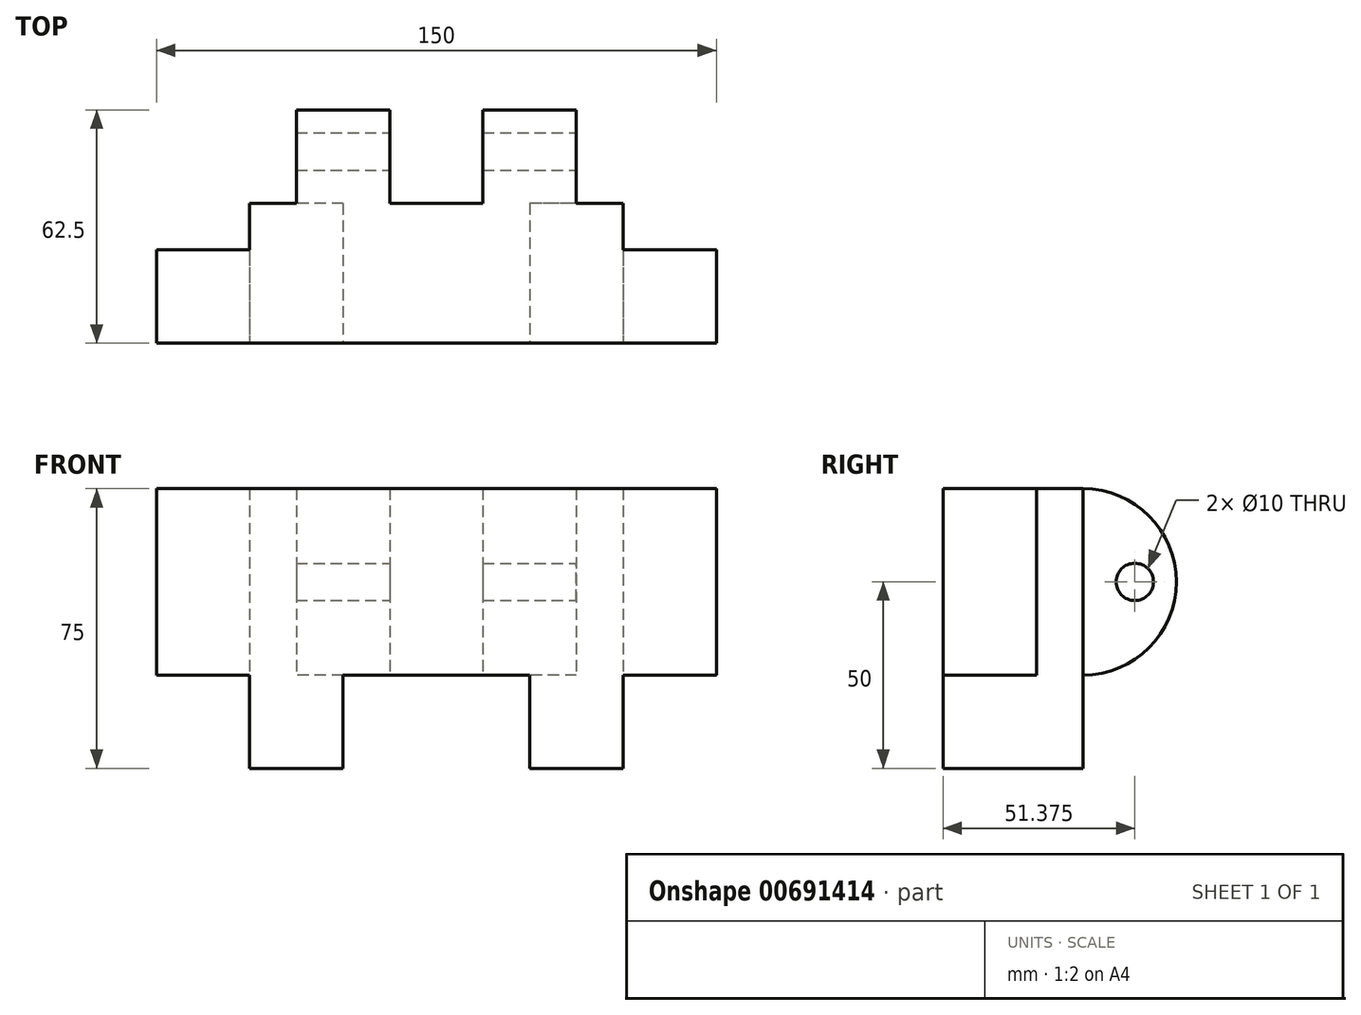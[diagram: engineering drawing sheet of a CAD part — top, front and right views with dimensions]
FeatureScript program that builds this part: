
annotation { "Feature Type Name" : "Feature", "Feature Type Description" : "" }
export const myFeature = defineFeature(function(context is Context, id is Id, definition is map)
    precondition{}
    {
        {
            var Q0;
            Q0=qCreatedBy(makeId("Top.planeOp"),FACE);
            var sketch = newSketch(context, id + "F0", { "sketchPlane" : qUnion([Q0])});
            skLineSegment(sketch, "E0.bottom", {"start": v(75, 12.5) * mm, "end": v(-75, 12.5) * mm});
            skLineSegment(sketch, "E0.top", {"start": v(75, -12.5) * mm, "end": v(-75, -12.5) * mm});
            skLineSegment(sketch, "E0.left", {"start": v(75, 12.5) * mm, "end": v(75, -12.5) * mm});
            skLineSegment(sketch, "E0.right", {"start": v(-75, 12.5) * mm, "end": v(-75, -12.5) * mm});
            skPoint(sketch, "E0.middle", {"position": v(0, 0) * mm});
            skLineSegment(sketch, "E1.bottom", {"start": v(50, 25) * mm, "end": v(-50, 25) * mm});
            skLineSegment(sketch, "E1.top", {"start": v(50, 0) * mm, "end": v(-50, 0) * mm});
            skLineSegment(sketch, "E1.left", {"start": v(50, 25) * mm, "end": v(50, 0) * mm});
            skLineSegment(sketch, "E1.right", {"start": v(-50, 25) * mm, "end": v(-50, 0) * mm});
            skPoint(sketch, "E1.middle", {"position": v(0, 12.5) * mm});
            skSolve(sketch);
        }
        {
            var Q0;
            Q0 = qSketchRegion(id + "F0", true);
            extrude(context, id + "F1", {"entities" : qUnion([Q0]), "depth" : 50 * mm, "offsetDistance" : 25 * mm});
        }
        {
            var Q0;
            Q0=makeQuery(id+"F1.opExtrude","SWEPT_FACE",FACE,{"disambiguationData":[OSD([sQuery(id+"F0.wireOp",EDGE,"E1.bottom")])]});
            var sketch = newSketch(context, id + "F2", { "sketchPlane" : qUnion([Q0])});
            skLineSegment(sketch, "E2.bottom", {"start": v(37.5, 50) * mm, "end": v(-37.5, 50) * mm});
            skLineSegment(sketch, "E2.top", {"start": v(37.5, 0) * mm, "end": v(-37.5, 0) * mm});
            skLineSegment(sketch, "E2.left", {"start": v(37.5, 50) * mm, "end": v(37.5, 0) * mm});
            skLineSegment(sketch, "E2.right", {"start": v(-37.5, 50) * mm, "end": v(-37.5, 0) * mm});
            skPoint(sketch, "E2.middle", {"position": v(0, 25) * mm});
            skPoint(sketch, "E2.middle.positionSnap0", {"position": v(50, 25) * mm});
            skPoint(sketch, "E2.centerSnap0", {"position": v(50, 25) * mm});
            skLineSegment(sketch, "E3.bottom", {"start": v(12.5, 50) * mm, "end": v(-12.5, 50) * mm});
            skLineSegment(sketch, "E3.top", {"start": v(12.5, 0) * mm, "end": v(-12.5, 0) * mm});
            skLineSegment(sketch, "E3.left", {"start": v(12.5, 50) * mm, "end": v(12.5, 0) * mm});
            skLineSegment(sketch, "E3.right", {"start": v(-12.5, 50) * mm, "end": v(-12.5, 0) * mm});
            skSolve(sketch);
        }
        {
            var Q0;
            {var subQ0=sQuery(id+"F2.wireOp",EDGE,"E2.right");Q0=makeQuery(id+"F2.imprint","IMPRINT",FACE,{"disambiguationData":[TD([[makeQuery(id+"F2.imprint","IMPRINT",EDGE,{"derivedFrom":subQ0}),1.0]])]});}
            var Q1;
            {var subQ0=sQuery(id+"F2.wireOp",EDGE,"E2.left");Q1=makeQuery(id+"F2.imprint","IMPRINT",FACE,{"disambiguationData":[TD([[makeQuery(id+"F2.imprint","IMPRINT",EDGE,{"derivedFrom":subQ0}),-1.0]])]});}
            extrude(context, id + "F3", {"entities" : qUnion([Q0, Q1]), "operationType" : NewBodyOperationType.ADD, "depth" : 25 * mm, "offsetDistance" : 25 * mm});
        }
        {
            var Q0;
            {var subQ0=sQuery(id+"F2.wireOp",EDGE,"E2.bottom");Q0=makeQuery(id+"F3.opExtrude","CAP_EDGE",EDGE,{"disambiguationData":[OSD([subQ0]),TDD([makeQuery(id+"F2.imprint","IMPRINT",EDGE,{"disambiguationData":[TD([[makeQuery(id+"F2.imprint","INTERSECT",VERTEX,{"derivedFrom":[makeQuery(id+"F1.opExtrude","CAP_EDGE",EDGE,{"disambiguationData":[OSD([sQuery(id+"F0.wireOp",EDGE,"E1.bottom")])],"isStart":false}),subQ0,sQuery(id+"F2.wireOp",EDGE,"E2.right")]}),-1.0]])],"derivedFrom":subQ0})])],"isStart":false});}
            var Q1;
            {var subQ0=sQuery(id+"F2.wireOp",EDGE,"E2.bottom");Q1=makeQuery(id+"F3.opExtrude","CAP_EDGE",EDGE,{"disambiguationData":[OSD([subQ0]),TDD([makeQuery(id+"F2.imprint","IMPRINT",EDGE,{"disambiguationData":[TD([[makeQuery(id+"F2.imprint","INTERSECT",VERTEX,{"derivedFrom":[makeQuery(id+"F1.opExtrude","CAP_EDGE",EDGE,{"disambiguationData":[OSD([sQuery(id+"F0.wireOp",EDGE,"E1.bottom")])],"isStart":false}),subQ0,sQuery(id+"F2.wireOp",EDGE,"E2.left")]}),1.0]])],"derivedFrom":subQ0})])],"isStart":false});}
            var Q2;
            {var subQ0=sQuery(id+"F2.wireOp",EDGE,"E2.top");Q2=makeQuery(id+"F3.opExtrude","CAP_EDGE",EDGE,{"disambiguationData":[OSD([subQ0]),TDD([makeQuery(id+"F2.imprint","IMPRINT",EDGE,{"disambiguationData":[TD([[makeQuery(id+"F2.imprint","INTERSECT",VERTEX,{"derivedFrom":[makeQuery(id+"F1.opExtrude","CAP_EDGE",EDGE,{"disambiguationData":[OSD([sQuery(id+"F0.wireOp",EDGE,"E1.bottom")])],"isStart":true}),subQ0,sQuery(id+"F2.wireOp",EDGE,"E2.left")]}),1.0]])],"derivedFrom":subQ0})])],"isStart":false});}
            var Q3;
            {var subQ0=sQuery(id+"F2.wireOp",EDGE,"E2.top");Q3=makeQuery(id+"F3.opExtrude","CAP_EDGE",EDGE,{"disambiguationData":[OSD([subQ0]),TDD([makeQuery(id+"F2.imprint","IMPRINT",EDGE,{"disambiguationData":[TD([[makeQuery(id+"F2.imprint","INTERSECT",VERTEX,{"derivedFrom":[makeQuery(id+"F1.opExtrude","CAP_EDGE",EDGE,{"disambiguationData":[OSD([sQuery(id+"F0.wireOp",EDGE,"E1.bottom")])],"isStart":true}),subQ0,sQuery(id+"F2.wireOp",EDGE,"E2.right")]}),-1.0]])],"derivedFrom":subQ0})])],"isStart":false});}
            fillet(context, id + "F4", {"entities" : qUnion([Q0, Q1, Q2, Q3]), "radius" : 25 * mm, "tangentPropagation" : true, "allowEdgeOverflow" : false});
        }
        {
            var Q0;
            Q0=makeQuery(id+"F3.opExtrude","SWEPT_FACE",FACE,{"disambiguationData":[OSD([sQuery(id+"F2.wireOp",EDGE,"E2.right")])]});
            var sketch = newSketch(context, id + "F5", { "sketchPlane" : qUnion([Q0])});
            skCircle(sketch, "E4", {"center": v(38.88, 25) * mm, "radius": 5 * mm});
            skPoint(sketch, "E4.centerSnap0", {"position": v(25, 25) * mm});
            skSolve(sketch);
        }
        {
            var Q0;
            Q0 = qSketchRegion(id + "F5", true);
            extrude(context, id + "F6", {"entities" : qUnion([Q0]), "operationType" : NewBodyOperationType.REMOVE, "endBound" : BoundingType.THROUGH_ALL, "oppositeDirection" : true, "depth" : 25 * mm, "offsetDistance" : 25 * mm});
        }
        {
            var Q0;
            {var subQ0=sQuery(id+"F2.wireOp",EDGE,"E2.bottom");var subQ1=sQuery(id+"F0.wireOp",EDGE,"E1.bottom");var subQ2=makeQuery(id+"F1.opExtrude","CAP_EDGE",EDGE,{"disambiguationData":[OSD([subQ1])],"isStart":false});Q0=makeQuery(id+"F3.boolean.opBoolean","MERGE",FACE,{"derivedFrom":[makeQuery(id+"F1.opExtrude","CAP_FACE",FACE,{"disambiguationData":[OSD([sQuery(id+"F0.wireOp",EDGE,"E0.bottom"),sQuery(id+"F0.wireOp",EDGE,"E0.top"),sQuery(id+"F0.wireOp",EDGE,"E0.left"),sQuery(id+"F0.wireOp",EDGE,"E0.right"),subQ1,sQuery(id+"F0.wireOp",EDGE,"E1.left"),sQuery(id+"F0.wireOp",EDGE,"E1.right")])],"isStart":false}),makeQuery(id+"F3.opExtrude","SWEPT_FACE",FACE,{"disambiguationData":[OSD([subQ0]),TDD([makeQuery(id+"F2.imprint","IMPRINT",EDGE,{"disambiguationData":[TD([[makeQuery(id+"F2.imprint","INTERSECT",VERTEX,{"derivedFrom":[subQ2,subQ0,sQuery(id+"F2.wireOp",EDGE,"E2.right")]}),-1.0]])],"derivedFrom":subQ0})])]}),makeQuery(id+"F3.opExtrude","SWEPT_FACE",FACE,{"disambiguationData":[OSD([subQ0]),TDD([makeQuery(id+"F2.imprint","IMPRINT",EDGE,{"disambiguationData":[TD([[makeQuery(id+"F2.imprint","INTERSECT",VERTEX,{"derivedFrom":[subQ2,subQ0,sQuery(id+"F2.wireOp",EDGE,"E2.left")]}),1.0]])],"derivedFrom":subQ0})])]})]});}
            var sketch = newSketch(context, id + "F7", { "sketchPlane" : qUnion([Q0])});
            skLineSegment(sketch, "E5.bottom", {"start": v(-50, 25) * mm, "end": v(50, 25) * mm});
            skLineSegment(sketch, "E5.top", {"start": v(-50, -12.5) * mm, "end": v(50, -12.5) * mm});
            skLineSegment(sketch, "E5.left", {"start": v(-50, 25) * mm, "end": v(-50, -12.5) * mm});
            skLineSegment(sketch, "E5.right", {"start": v(50, 25) * mm, "end": v(50, -12.5) * mm});
            skLineSegment(sketch, "E6.bottom", {"start": v(-25, 25) * mm, "end": v(25, 25) * mm});
            skLineSegment(sketch, "E6.top", {"start": v(-25, -12.5) * mm, "end": v(25, -12.5) * mm});
            skLineSegment(sketch, "E6.left", {"start": v(-25, 25) * mm, "end": v(-25, -12.5) * mm});
            skLineSegment(sketch, "E6.right", {"start": v(25, 25) * mm, "end": v(25, -12.5) * mm});
            skPoint(sketch, "E6.middle", {"position": v(0, 6.25) * mm});
            skPoint(sketch, "E6.middle.positionSnap0", {"position": v(-50, 6.25) * mm});
            skPoint(sketch, "E6.centerSnap0", {"position": v(-50, 6.25) * mm});
            skLineSegment(sketch, "E7.top", {"start": v(-25, -2.5) * mm, "end": v(25, -2.5) * mm});
            skLineSegment(sketch, "E7.left", {"start": v(-25, -12.5) * mm, "end": v(-25, -2.5) * mm});
            skLineSegment(sketch, "E7.right", {"start": v(25, -12.5) * mm, "end": v(25, -2.5) * mm});
            skSolve(sketch);
        }
        {
            var Q0;
            {var subQ8=sQuery(id+"F7.wireOp",EDGE,"E6.right");Q0=makeQuery(id+"F7.imprint","IMPRINT",FACE,{"disambiguationData":[TD([[makeQuery(id+"F7.imprint","IMPRINT",EDGE,{"derivedFrom":subQ8}),1.0]])]});}
            var Q1;
            Q1=makeQuery(id+"F7.imprint","IMPRINT",FACE,{"disambiguationData":[TD([[makeQuery(id+"F7.imprint","IMPRINT",EDGE,{"derivedFrom":sQuery(id+"F7.wireOp",EDGE,"E6.top")}),-1.0]])]});
            var Q2;
            {var subQ8=sQuery(id+"F7.wireOp",EDGE,"E6.left");Q2=makeQuery(id+"F7.imprint","IMPRINT",FACE,{"disambiguationData":[TD([[makeQuery(id+"F7.imprint","IMPRINT",EDGE,{"derivedFrom":subQ8}),-1.0]])]});}
            extrude(context, id + "F8", {"entities" : qUnion([Q0, Q1, Q2]), "operationType" : NewBodyOperationType.ADD, "oppositeDirection" : true, "depth" : 75 * mm, "offsetDistance" : 25 * mm});
        }
    });
